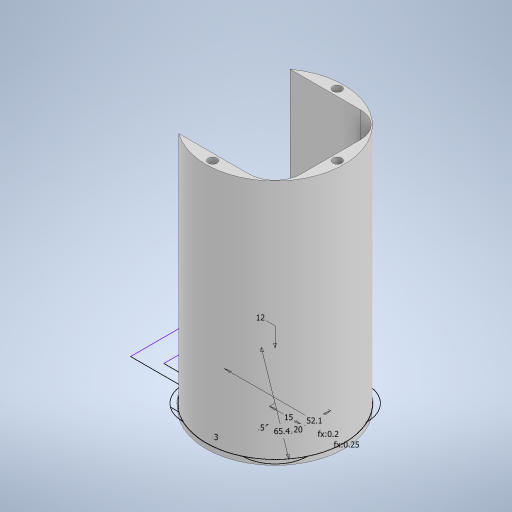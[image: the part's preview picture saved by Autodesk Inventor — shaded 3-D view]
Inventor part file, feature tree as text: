
AUTODESK INVENTOR PART (.ipt)
format: ipt  version: 2023 (Build 270158000, 158)  size: 338,432 bytes
history: native  units: in
note: dims shown in document units (in); Inventor stores cm internally (conversion verified against a paired STEP export)
features: extrude x6, sketch x4, chamfer x3, projected_geometry x2, fillet x1, mirror x1
ambient origin geometry x8: Origin, YZ Plane, XZ Plane, XY Plane, X Axis, Y Axis, Z Axis, Center Point
bodies: Solid1 (feature_tree)
feature tree (17):
  sketch  "Sketch1"  dims[d0=2.5748in d1=0.0098in]
  extrude  "Extrusion1"  Depth=0.0098in
  extrude  "Extrusion2"  Depth=0.4724in
  extrude  "Extrusion3"  Depth=0.5906in
  fillet  "Fillet1"  Radius=0.5906in
  chamfer  "Chamfer1"  Distance=0.1969in
  extrude  "Extrusion4"  Depth=0.0984in TaperAngle=0.0deg
  chamfer  "Chamfer2"  Distance=0.0984in
  extrude  "Extrusion5"  Depth=0.3937in TaperAngle=0.0deg
  chamfer  "Chamfer3"  Distance=0.0197in
  extrude  "Extrusion6"  Depth=0.5906in TaperAngle=45.0deg
  mirror  "Mirror1"
  sketch  "Sketch3"  dims[d2=2.0512in d3=0.4724in]
  sketch  "Sketch4"  dims[d4=0.0984in d5=0.0in d6=0.0079in d7=0.5906in]
  projected_geometry  "Projected Loop1"
  sketch  "Sketch5"  dims[d8=0.7874in d9=0.1969in d10=0.0984in d11=0.0in d12=0.0984in d13=0.3937in d14=0.0in d15=0.0197in d16=0.0512in d17=0.0787in d18=45.0deg d19=0.1181in d20=4.4724in d21=0.0in d22=0.0512in d23=0.0787in d24=45.0deg d25=0.0512in d26=0.0394in d27=0.0in d28=0.0512in d29=0.0787in d30=45.0deg d31=0.1654in d32=0.5906in d33=0.0in d34=0.0344in]
  projected_geometry  "Projected Loop2"
